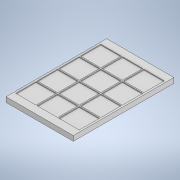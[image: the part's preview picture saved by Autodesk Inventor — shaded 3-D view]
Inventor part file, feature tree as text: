
AUTODESK INVENTOR PART (.ipt)
format: ipt  version: 2020 (Build 240168000, 168)  size: 150,016 bytes
history: native  units: in
note: dims shown in document units (in); Inventor stores cm internally (conversion verified against a paired STEP export)
features: extrude x2, sketch x2, pattern_linear x1
ambient origin geometry x8: Origin, YZ Plane, XZ Plane, XY Plane, X Axis, Y Axis, Z Axis, Center Point
bodies: Solid1 (feature_tree)
feature tree (5):
  extrude  "Extrusion1"  Depth=5.0299in
  extrude  "Extrusion2"  Depth=1.0787in
  pattern_linear  "Rectangular Pattern2"  Spacing1=0.25in  [1 undecoded]
  sketch  "Sketch1"  dims[d0=3.3654in d1=5.0299in]
  sketch  "Sketch3"  dims[d3=45.0deg d4=0.375in d5=0.25in d6=0.0in d23=0.094in d24=0.387in d25=1.0197in d26=1.0197in d27=0.0394in d28=0.0394in d29=0.0394in d30=0.0in d31=1.1811in d33=1.0787in d34=1.5748in d36=1.0787in]
note: 1 required parameter value undecoded (feature->parameter linkage not recoverable at this tier; creation-order binding heuristic only, values carry confidence <= 0.55)
